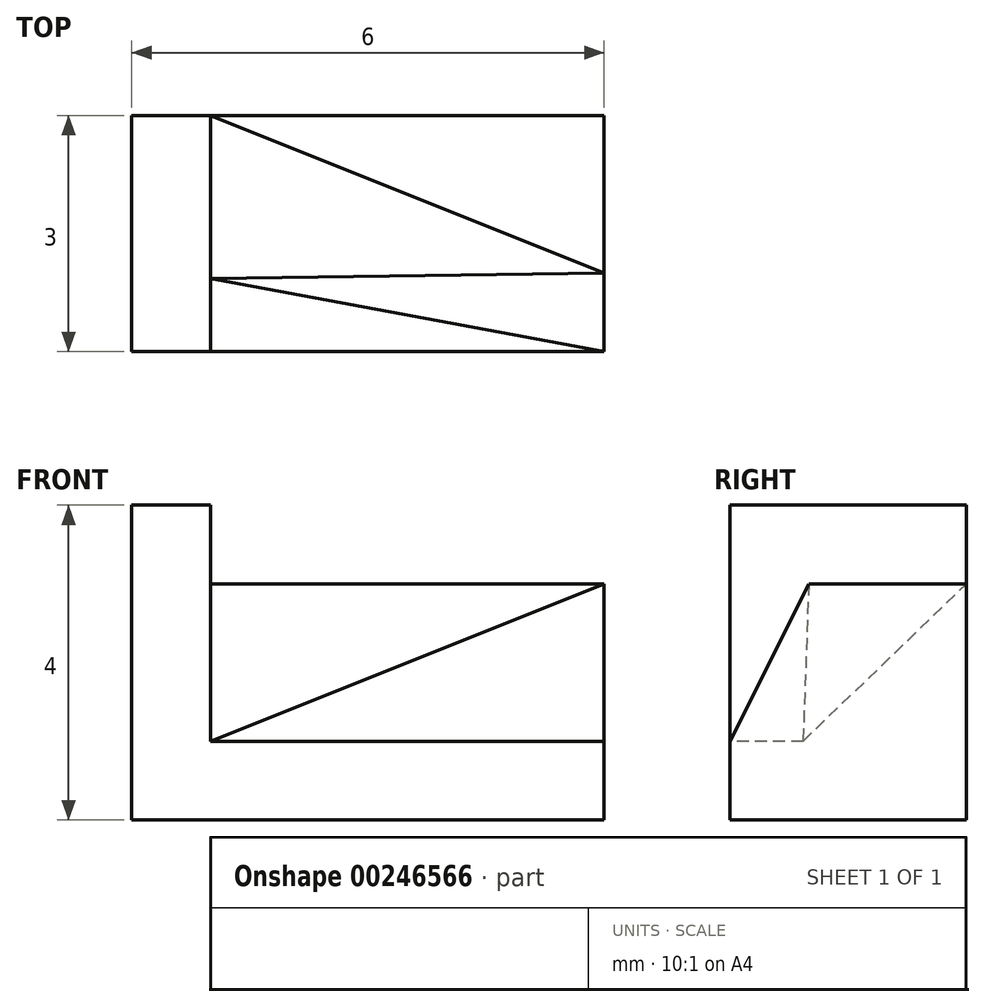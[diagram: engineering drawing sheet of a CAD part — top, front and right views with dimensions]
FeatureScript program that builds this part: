
annotation { "Feature Type Name" : "Feature", "Feature Type Description" : "" }
export const myFeature = defineFeature(function(context is Context, id is Id, definition is map)
    precondition{}
    {
        {
            var Q0;
            Q0=qCreatedBy(makeId("Top.planeOp"),FACE);
            var sketch = newSketch(context, id + "F0", { "sketchPlane" : qUnion([Q0])});
            skLineSegment(sketch, "E0.bottom", {"start": v(0, 0) * mm, "end": v(6, 0) * mm});
            skLineSegment(sketch, "E0.top", {"start": v(0, 3) * mm, "end": v(6, 3) * mm});
            skLineSegment(sketch, "E0.left", {"start": v(0, 0) * mm, "end": v(0, 3) * mm});
            skLineSegment(sketch, "E0.right", {"start": v(6, 0) * mm, "end": v(6, 3) * mm});
            skSolve(sketch);
        }
        {
            var Q0;
            Q0=makeQuery(id+"F0.imprint","IMPRINT",FACE,{"disambiguationData":[TD([[makeQuery(id+"F0.imprint","IMPRINT",EDGE,{"derivedFrom":sQuery(id+"F0.wireOp",EDGE,"E0.bottom")}),1.0]])]});
            extrude(context, id + "F1", {"entities" : qUnion([Q0]), "depth" : 3 * mm});
        }
        {
            var Q0;
            Q0=makeQuery(id+"F1.opExtrude","CAP_FACE",FACE,{"disambiguationData":[OSD([sQuery(id+"F0.wireOp",EDGE,"E0.bottom"),sQuery(id+"F0.wireOp",EDGE,"E0.top"),sQuery(id+"F0.wireOp",EDGE,"E0.left"),sQuery(id+"F0.wireOp",EDGE,"E0.right")])],"isStart":false});
            var sketch = newSketch(context, id + "F2", { "sketchPlane" : qUnion([Q0])});
            skLineSegment(sketch, "E1.bottom", {"start": v(0, 3) * mm, "end": v(1, 3) * mm});
            skLineSegment(sketch, "E1.top", {"start": v(0, 0) * mm, "end": v(1, 0) * mm});
            skLineSegment(sketch, "E1.left", {"start": v(0, 3) * mm, "end": v(0, 0) * mm});
            skLineSegment(sketch, "E1.right", {"start": v(1, 3) * mm, "end": v(1, 0) * mm});
            skSolve(sketch);
        }
        {
            var Q0;
            Q0=makeQuery(id+"F2.imprint","IMPRINT",FACE,{"disambiguationData":[TD([[makeQuery(id+"F2.imprint","IMPRINT",EDGE,{"derivedFrom":sQuery(id+"F2.wireOp",EDGE,"E1.bottom")}),-1.0]])]});
            extrude(context, id + "F3", {"entities" : qUnion([Q0]), "operationType" : NewBodyOperationType.ADD, "depth" : 1 * mm});
        }
        {
            var Q0;
            Q0=makeQuery(id+"F1.opExtrude","CAP_FACE",FACE,{"disambiguationData":[OSD([sQuery(id+"F0.wireOp",EDGE,"E0.bottom"),sQuery(id+"F0.wireOp",EDGE,"E0.top"),sQuery(id+"F0.wireOp",EDGE,"E0.left"),sQuery(id+"F0.wireOp",EDGE,"E0.right")])],"isStart":false});
            var sketch = newSketch(context, id + "F4", { "sketchPlane" : qUnion([Q0])});
            skLineSegment(sketch, "E2", {"start": v(1, 0) * mm, "end": v(1, 0.93) * mm});
            skLineSegment(sketch, "E3", {"start": v(1, 0.93) * mm, "end": v(6, 0) * mm});
            skLineSegment(sketch, "E4", {"start": v(1, 0) * mm, "end": v(6, 0) * mm});
            skSolve(sketch);
        }
        {
            var Q0;
            Q0=makeQuery(id+"F4.imprint","IMPRINT",FACE,{"disambiguationData":[TD([[makeQuery(id+"F4.imprint","IMPRINT",EDGE,{"derivedFrom":sQuery(id+"F4.wireOp",EDGE,"E2")}),1.0]])]});
            extrude(context, id + "F5", {"entities" : qUnion([Q0]), "operationType" : NewBodyOperationType.REMOVE, "oppositeDirection" : true, "depth" : 2 * mm});
        }
        {
            var Q0;
            Q0=makeQuery(id+"F1.opExtrude","CAP_FACE",FACE,{"disambiguationData":[OSD([sQuery(id+"F0.wireOp",EDGE,"E0.bottom"),sQuery(id+"F0.wireOp",EDGE,"E0.top"),sQuery(id+"F0.wireOp",EDGE,"E0.left"),sQuery(id+"F0.wireOp",EDGE,"E0.right")])],"isStart":false});
            var sketch = newSketch(context, id + "F6", { "sketchPlane" : qUnion([Q0])});
            skLineSegment(sketch, "E5", {"start": v(1, 3) * mm, "end": v(6, 3) * mm});
            skLineSegment(sketch, "E6", {"start": v(6, 1) * mm, "end": v(6, 3) * mm});
            skLineSegment(sketch, "E7", {"start": v(1, 3) * mm, "end": v(6, 1) * mm});
            skSolve(sketch);
        }
        {
            var Q0;
            Q0=sQuery(id+"F6.wireOp",VERTEX,"E7.start");
            var Q1;
            Q1=makeQuery(id+"F5.boolean.opBoolean","COPY",VERTEX,{"derivedFrom":makeQuery(id+"F5.opExtrude","CAP_VERTEX",VERTEX,{"disambiguationData":[OSD([sQuery(id+"F2.wireOp",EDGE,"E1.right"),sQuery(id+"F4.wireOp",EDGE,"E2"),sQuery(id+"F4.wireOp",EDGE,"E3")])],"isStart":false})});
            var Q2;
            Q2=sQuery(id+"F6.wireOp",VERTEX,"E7.end");
            cPlane(context, id + "F7", {"entities" : qUnion([Q0, Q1, Q2]), "cplaneType" : CPlaneType.THREE_POINT, "offset" : 25 * mm, "width" : 150 * mm, "height" : 150 * mm});
        }
        {
            var Q0;
            Q0=qCreatedBy(id+"F7.planeOp",FACE);
            var sketch = newSketch(context, id + "F8", { "sketchPlane" : qUnion([Q0])});
            skPoint(sketch, "E8.0", {"position": v(0.98, -4.24) * mm});
            skPoint(sketch, "E8.1", {"position": v(6.17, -2.8) * mm});
            skPoint(sketch, "E8.2", {"position": v(0.98, -1.36) * mm});
            skLineSegment(sketch, "E9", {"start": v(0.98, -4.24) * mm, "end": v(6.17, -2.8) * mm});
            skLineSegment(sketch, "E10", {"start": v(6.17, -2.8) * mm, "end": v(0.98, -1.36) * mm});
            skLineSegment(sketch, "E11", {"start": v(0.98, -1.36) * mm, "end": v(0.98, -4.24) * mm});
            skSolve(sketch);
        }
        {
            var Q0;
            Q0=makeQuery(id+"F3.opExtrude","CAP_FACE",FACE,{"disambiguationData":[OSD([sQuery(id+"F2.wireOp",EDGE,"E1.bottom"),sQuery(id+"F2.wireOp",EDGE,"E1.top"),sQuery(id+"F2.wireOp",EDGE,"E1.left"),sQuery(id+"F2.wireOp",EDGE,"E1.right")])],"isStart":false});
            extrude(context, id + "F9", {"entities" : qUnion([Q0]), "operationType" : NewBodyOperationType.REMOVE, "oppositeDirection" : true, "depth" : 3 * mm});
        }
        {
            var Q0;
            Q0 = qSketchRegion(id + "F8", true);
            extrude(context, id + "F10", {"entities" : qUnion([Q0]), "operationType" : NewBodyOperationType.REMOVE, "oppositeDirection" : true, "depth" : 25 * mm});
        }
        {
            var Q0;
            Q0=sQuery(id+"F6.wireOp",VERTEX,"E7.end");
            var Q1;
            Q1=makeQuery(id+"F10.boolean.opBoolean","MERGE",VERTEX,{"derivedFrom":[makeQuery(id+"F5.boolean.opBoolean","COPY",VERTEX,{"derivedFrom":makeQuery(id+"F5.opExtrude","CAP_VERTEX",VERTEX,{"disambiguationData":[OSD([sQuery(id+"F2.wireOp",EDGE,"E1.right"),sQuery(id+"F4.wireOp",EDGE,"E2"),sQuery(id+"F4.wireOp",EDGE,"E3")])],"isStart":false})}),makeQuery(id+"F10.opExtrude","CAP_VERTEX",VERTEX,{"disambiguationData":[OSD([sQuery(id+"F8.wireOp",EDGE,"E10"),sQuery(id+"F8.wireOp",EDGE,"E11")])],"isStart":true})]});
            var Q2;
            Q2=makeQuery(id+"F5.boolean.opBoolean","COPY",VERTEX,{"derivedFrom":makeQuery(id+"F5.opExtrude","CAP_VERTEX",VERTEX,{"disambiguationData":[OSD([sQuery(id+"F0.wireOp",EDGE,"E0.right"),sQuery(id+"F4.wireOp",EDGE,"E3"),sQuery(id+"F4.wireOp",EDGE,"E4")])],"isStart":false})});
            cPlane(context, id + "F11", {"entities" : qUnion([Q0, Q1, Q2]), "cplaneType" : CPlaneType.THREE_POINT, "offset" : 25 * mm, "width" : 150 * mm, "height" : 150 * mm});
        }
        {
            var Q0;
            Q0=sQuery(id+"F6.wireOp",VERTEX,"E7.end");
            var Q1;
            Q1=makeQuery(id+"F5.boolean.opBoolean","COPY",VERTEX,{"derivedFrom":makeQuery(id+"F5.opExtrude","CAP_VERTEX",VERTEX,{"disambiguationData":[OSD([sQuery(id+"F0.wireOp",EDGE,"E0.right"),sQuery(id+"F4.wireOp",EDGE,"E3"),sQuery(id+"F4.wireOp",EDGE,"E4")])],"isStart":false})});
            var Q2;
            Q2=makeQuery(id+"F10.boolean.opBoolean","MERGE",VERTEX,{"derivedFrom":[makeQuery(id+"F5.boolean.opBoolean","COPY",VERTEX,{"derivedFrom":makeQuery(id+"F5.opExtrude","CAP_VERTEX",VERTEX,{"disambiguationData":[OSD([sQuery(id+"F2.wireOp",EDGE,"E1.right"),sQuery(id+"F4.wireOp",EDGE,"E2"),sQuery(id+"F4.wireOp",EDGE,"E3")])],"isStart":false})}),makeQuery(id+"F10.opExtrude","CAP_VERTEX",VERTEX,{"disambiguationData":[OSD([sQuery(id+"F8.wireOp",EDGE,"E10"),sQuery(id+"F8.wireOp",EDGE,"E11")])],"isStart":true})]});
            cPlane(context, id + "F12", {"entities" : qUnion([Q0, Q1, Q2]), "cplaneType" : CPlaneType.THREE_POINT, "offset" : 25 * mm, "width" : 150 * mm, "height" : 150 * mm});
        }
        {
            var Q0;
            Q0=qCreatedBy(id+"F12.planeOp",FACE);
            var sketch = newSketch(context, id + "F13", { "sketchPlane" : qUnion([Q0])});
            skPoint(sketch, "E12.0", {"position": v(6, 3.13) * mm});
            skPoint(sketch, "E12.1", {"position": v(6, 0.9) * mm});
            skPoint(sketch, "E12.2", {"position": v(0.92, 1.3) * mm});
            skLineSegment(sketch, "E13", {"start": v(0.92, 1.3) * mm, "end": v(6, 0.9) * mm});
            skLineSegment(sketch, "E14", {"start": v(6, 0.9) * mm, "end": v(6.72, 0.9) * mm});
            skLineSegment(sketch, "E15", {"start": v(6.72, 0.9) * mm, "end": v(6.27, 3.7) * mm});
            skLineSegment(sketch, "E16", {"start": v(6.27, 3.7) * mm, "end": v(1.1, 3.29) * mm});
            skLineSegment(sketch, "E17", {"start": v(1.1, 3.29) * mm, "end": v(0.92, 1.3) * mm});
            skSolve(sketch);
        }
        {
            var Q0;
            Q0 = qSketchRegion(id + "F13", true);
            extrude(context, id + "F14", {"entities" : qUnion([Q0]), "operationType" : NewBodyOperationType.REMOVE, "depth" : 25 * mm});
        }
        {
            var Q0;
            Q0=makeQuery(id+"F9.boolean.opBoolean","MERGE",FACE,{"derivedFrom":[makeQuery(id+"F5.boolean.opBoolean","COPY",FACE,{"derivedFrom":makeQuery(id+"F5.opExtrude","CAP_FACE",FACE,{"disambiguationData":[OSD([sQuery(id+"F4.wireOp",EDGE,"E2"),sQuery(id+"F4.wireOp",EDGE,"E3"),sQuery(id+"F4.wireOp",EDGE,"E4")])],"isStart":false})}),makeQuery(id+"F9.opExtrude","CAP_FACE",FACE,{"disambiguationData":[OSD([sQuery(id+"F2.wireOp",EDGE,"E1.bottom"),sQuery(id+"F2.wireOp",EDGE,"E1.top"),sQuery(id+"F2.wireOp",EDGE,"E1.left"),sQuery(id+"F2.wireOp",EDGE,"E1.right")])],"isStart":false})]});
            var sketch = newSketch(context, id + "F15", { "sketchPlane" : qUnion([Q0])});
            skLineSegment(sketch, "E18.bottom", {"start": v(0, 3) * mm, "end": v(1, 3) * mm});
            skLineSegment(sketch, "E18.top", {"start": v(0, 0) * mm, "end": v(1, 0) * mm});
            skLineSegment(sketch, "E18.left", {"start": v(0, 3) * mm, "end": v(0, 0) * mm});
            skLineSegment(sketch, "E18.right", {"start": v(1, 3) * mm, "end": v(1, 0) * mm});
            skSolve(sketch);
        }
        {
            var Q0;
            Q0 = qSketchRegion(id + "F15", true);
            extrude(context, id + "F16", {"entities" : qUnion([Q0]), "operationType" : NewBodyOperationType.ADD, "depth" : 3 * mm});
        }
    });
